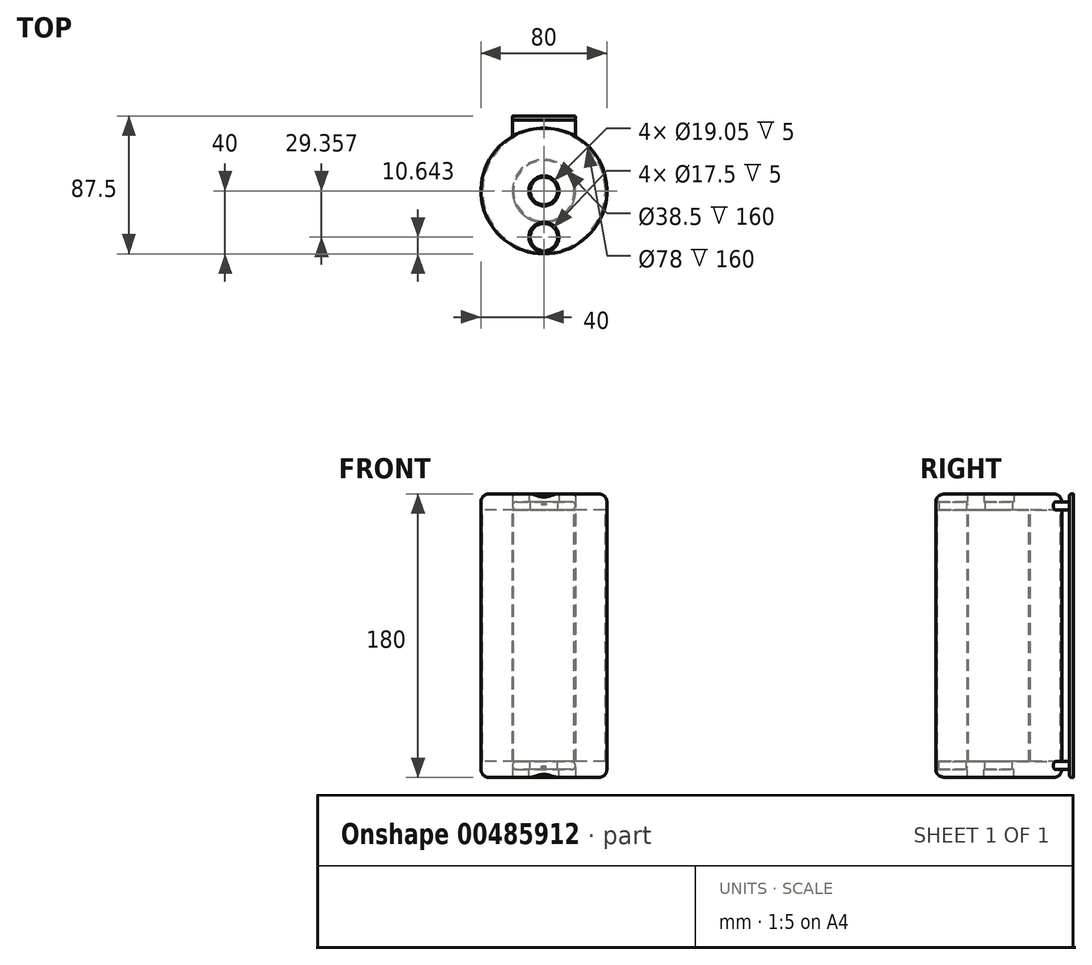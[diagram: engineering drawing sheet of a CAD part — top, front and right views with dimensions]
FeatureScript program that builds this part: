
annotation { "Feature Type Name" : "Feature", "Feature Type Description" : "" }
export const myFeature = defineFeature(function(context is Context, id is Id, definition is map)
    precondition{}
    {
        {
            var Q0;
            Q0=qCreatedBy(makeId("Top.planeOp"),FACE);
            var sketch = newSketch(context, id + "F0", { "sketchPlane" : qUnion([Q0])});
            skCircle(sketch, "E0", {"center": v(0, 0) * mm, "radius": 40 * mm});
            skLineSegment(sketch, "E1", {"start": v(0, 0) * mm, "end": v(0, -20) * mm});
            skLineSegment(sketch, "E2", {"start": v(0, -20) * mm, "end": v(0, -21.21) * mm});
            skLineSegment(sketch, "E3", {"start": v(0, -21.21) * mm, "end": v(0, -37.5) * mm});
            skLineSegment(sketch, "E4", {"start": v(0, -37.5) * mm, "end": v(0, -29.36) * mm});
            skCircle(sketch, "E5", {"center": v(0, -29.36) * mm, "radius": 9.53 * mm});
            skCircle(sketch, "E6", {"center": v(0, 0) * mm, "radius": 9.53 * mm});
            skCircle(sketch, "E7", {"center": v(0, 0) * mm, "radius": 20 * mm});
            skCircle(sketch, "E8", {"center": v(0, 0) * mm, "radius": 19.25 * mm});
            skCircle(sketch, "E9", {"center": v(0, -29.36) * mm, "radius": 8.75 * mm});
            skCircle(sketch, "E10", {"center": v(0, 0) * mm, "radius": 8.75 * mm});
            skCircle(sketch, "E11", {"center": v(0, 0) * mm, "radius": 39 * mm});
            skLineSegment(sketch, "E12.top", {"start": v(20, 40) * mm, "end": v(0, 40) * mm});
            skLineSegment(sketch, "E13.top", {"start": v(0, 40) * mm, "end": v(-20, 40) * mm});
            skLineSegment(sketch, "E14", {"start": v(-20, 34.64) * mm, "end": v(-20, 40) * mm});
            skLineSegment(sketch, "E15", {"start": v(20, 40) * mm, "end": v(20, 34.64) * mm});
            skLineSegment(sketch, "E16.bottom", {"start": v(-20, 40) * mm, "end": v(20, 40) * mm});
            skLineSegment(sketch, "E16.top", {"start": v(-20, 45) * mm, "end": v(20, 45) * mm});
            skLineSegment(sketch, "E16.left", {"start": v(-20, 40) * mm, "end": v(-20, 45) * mm});
            skLineSegment(sketch, "E16.right", {"start": v(20, 40) * mm, "end": v(20, 45) * mm});
            skLineSegment(sketch, "E17.top", {"start": v(-20, 47.5) * mm, "end": v(20, 47.5) * mm});
            skLineSegment(sketch, "E17.left", {"start": v(-20, 45) * mm, "end": v(-20, 47.5) * mm});
            skLineSegment(sketch, "E17.right", {"start": v(20, 45) * mm, "end": v(20, 47.5) * mm});
            skSolve(sketch);
        }
        {
            var Q0;
            Q0=makeQuery(id+"F0.imprint","IMPRINT",FACE,{"disambiguationData":[TD([[makeQuery(id+"F0.imprint","IMPRINT",EDGE,{"derivedFrom":sQuery(id+"F0.wireOp",EDGE,"E11")}),1.0]])]});
            var Q1;
            Q1=makeQuery(id+"F0.imprint","IMPRINT",FACE,{"disambiguationData":[TD([[makeQuery(id+"F0.imprint","IMPRINT",EDGE,{"derivedFrom":sQuery(id+"F0.wireOp",EDGE,"E11")}),-1.0]])]});
            var Q2;
            Q2=makeQuery(id+"F0.imprint","IMPRINT",FACE,{"disambiguationData":[TD([[makeQuery(id+"F0.imprint","IMPRINT",EDGE,{"derivedFrom":sQuery(id+"F0.wireOp",EDGE,"E6")}),1.0]])]});
            var Q3;
            Q3=makeQuery(id+"F0.imprint","IMPRINT",FACE,{"disambiguationData":[TD([[makeQuery(id+"F0.imprint","IMPRINT",EDGE,{"derivedFrom":sQuery(id+"F0.wireOp",EDGE,"E6")}),-1.0]])]});
            var Q4;
            Q4=makeQuery(id+"F0.imprint","IMPRINT",FACE,{"disambiguationData":[TD([[makeQuery(id+"F0.imprint","IMPRINT",EDGE,{"derivedFrom":sQuery(id+"F0.wireOp",EDGE,"E8")}),-1.0]])]});
            var Q5;
            Q5=makeQuery(id+"F0.imprint","IMPRINT",FACE,{"disambiguationData":[TD([[makeQuery(id+"F0.imprint","IMPRINT",EDGE,{"derivedFrom":sQuery(id+"F0.wireOp",EDGE,"E9")}),-1.0]])]});
            extrude(context, id + "F1", {"entities" : qUnion([Q0, Q1, Q2, Q3, Q4, Q5]), "oppositeDirection" : true, "depth" : 10 * mm});
        }
        {
            var Q0;
            Q0=qSketchRegion(id+"FNYP8afO0flnPvm_4",true);
            var Q1;
            Q1=makeQuery(id+"F0.imprint","IMPRINT",FACE,{"disambiguationData":[TD([[makeQuery(id+"F0.imprint","IMPRINT",EDGE,{"derivedFrom":sQuery(id+"F0.wireOp",EDGE,"E11")}),-1.0]])]});
            var Q2;
            Q2=makeQuery(id+"F0.imprint","IMPRINT",FACE,{"disambiguationData":[TD([[makeQuery(id+"F0.imprint","IMPRINT",EDGE,{"derivedFrom":sQuery(id+"F0.wireOp",EDGE,"E8")}),-1.0]])]});
            extrude(context, id + "F2", {"entities" : qUnion([Q0, Q1, Q2]), "operationType" : NewBodyOperationType.REMOVE, "oppositeDirection" : true, "depth" : 4 * mm});
        }
        {
            var Q0;
            Q0=makeQuery(id+"F0.imprint","IMPRINT",FACE,{"disambiguationData":[TD([[makeQuery(id+"F0.imprint","IMPRINT",EDGE,{"derivedFrom":sQuery(id+"F0.wireOp",EDGE,"E6")}),1.0]])]});
            var Q1;
            {var subQ0=sQuery(id+"F0.wireOp",EDGE,"E7");var subQ1=sQuery(id+"F0.wireOp",EDGE,"E1");var subQ2=makeQuery(id+"F0.imprint","INTERSECT",VERTEX,{"derivedFrom":[subQ1,subQ0]});Q1=makeQuery(id+"F0.imprint","IMPRINT",FACE,{"disambiguationData":[TD([[makeQuery(id+"F0.imprint","IMPRINT",EDGE,{"disambiguationData":[TD([[subQ2,1.0]])],"derivedFrom":subQ1}),1.0]])]});}
            var Q2;
            {var subQ0=sQuery(id+"F0.wireOp",EDGE,"E7");var subQ1=sQuery(id+"F0.wireOp",EDGE,"E1");var subQ2=makeQuery(id+"F0.imprint","INTERSECT",VERTEX,{"derivedFrom":[subQ1,subQ0]});Q2=makeQuery(id+"F0.imprint","IMPRINT",FACE,{"disambiguationData":[TD([[makeQuery(id+"F0.imprint","IMPRINT",EDGE,{"disambiguationData":[TD([[subQ2,1.0]])],"derivedFrom":subQ1}),-1.0]])]});}
            var Q3;
            Q3=makeQuery(id+"F0.imprint","IMPRINT",FACE,{"disambiguationData":[TD([[makeQuery(id+"F0.imprint","IMPRINT",EDGE,{"derivedFrom":sQuery(id+"F0.wireOp",EDGE,"E9")}),-1.0]])]});
            extrude(context, id + "F3", {"entities" : qUnion([Q0, Q1, Q2, Q3]), "operationType" : NewBodyOperationType.REMOVE, "oppositeDirection" : true, "depth" : 10 * mm, "hasSecondDirection" : true, "secondDirectionOppositeDirection" : true, "secondDirectionDepth" : 5 * mm});
        }
        {
            var Q0;
            Q0=makeQuery(id+"F1.opExtrude","CAP_EDGE",EDGE,{"disambiguationData":[OSD([sQuery(id+"F0.wireOp",EDGE,"E0")])],"isStart":false});
            fillet(context, id + "F4", {"entities" : qUnion([Q0]), "radius" : 5 * mm, "tangentPropagation" : true, "allowEdgeOverflow" : false});
        }
        {
            var Q0;
            {var subQ0=sQuery(id+"F0.wireOp",EDGE,"E7");var subQ1=sQuery(id+"F0.wireOp",EDGE,"E1");var subQ2=makeQuery(id+"F0.imprint","INTERSECT",VERTEX,{"derivedFrom":[subQ1,subQ0]});Q0=makeQuery(id+"F0.imprint","IMPRINT",FACE,{"disambiguationData":[TD([[makeQuery(id+"F0.imprint","IMPRINT",EDGE,{"disambiguationData":[TD([[subQ2,1.0]])],"derivedFrom":subQ1}),-1.0]])]});}
            var Q1;
            {var subQ0=sQuery(id+"F0.wireOp",EDGE,"E7");var subQ1=sQuery(id+"F0.wireOp",EDGE,"E1");var subQ2=makeQuery(id+"F0.imprint","INTERSECT",VERTEX,{"derivedFrom":[subQ1,subQ0]});Q1=makeQuery(id+"F0.imprint","IMPRINT",FACE,{"disambiguationData":[TD([[makeQuery(id+"F0.imprint","IMPRINT",EDGE,{"disambiguationData":[TD([[subQ2,1.0]])],"derivedFrom":subQ1}),1.0]])]});}
            extrude(context, id + "F5", {"entities" : qUnion([Q0, Q1]), "operationType" : NewBodyOperationType.ADD, "oppositeDirection" : true, "depth" : 5 * mm, "hasSecondDirection" : true, "secondDirectionOppositeDirection" : true, "secondDirectionDepth" : 4 * mm});
        }
        {
            var Q0;
            Q0=makeQuery(id+"F0.imprint","IMPRINT",FACE,{"disambiguationData":[TD([[makeQuery(id+"F0.imprint","IMPRINT",EDGE,{"derivedFrom":sQuery(id+"F0.wireOp",EDGE,"E11")}),-1.0]])]});
            var Q1;
            Q1=makeQuery(id+"F0.imprint","IMPRINT",FACE,{"disambiguationData":[TD([[makeQuery(id+"F0.imprint","IMPRINT",EDGE,{"derivedFrom":sQuery(id+"F0.wireOp",EDGE,"E8")}),-1.0]])]});
            extrude(context, id + "F6", {"entities" : qUnion([Q0, Q1]), "oppositeDirection" : true, "depth" : 4 * mm, "hasSecondDirection" : true, "secondDirectionOppositeDirection" : true, "secondDirectionDepth" : 3 * mm});
        }
        {
            var Q0;
            Q0=makeQuery(id+"F0.imprint","IMPRINT",FACE,{"disambiguationData":[TD([[makeQuery(id+"F0.imprint","IMPRINT",EDGE,{"derivedFrom":sQuery(id+"F0.wireOp",EDGE,"E11")}),-1.0]])]});
            var Q1;
            Q1=makeQuery(id+"F0.imprint","IMPRINT",FACE,{"disambiguationData":[TD([[makeQuery(id+"F0.imprint","IMPRINT",EDGE,{"derivedFrom":sQuery(id+"F0.wireOp",EDGE,"E8")}),-1.0]])]});
            var Q2;
            {var subQ0=sQuery(id+"F0.wireOp",EDGE,"E7");var subQ1=sQuery(id+"F0.wireOp",EDGE,"E1");var subQ2=makeQuery(id+"F0.imprint","INTERSECT",VERTEX,{"derivedFrom":[subQ1,subQ0]});Q2=makeQuery(id+"F0.imprint","IMPRINT",FACE,{"disambiguationData":[TD([[makeQuery(id+"F0.imprint","IMPRINT",EDGE,{"disambiguationData":[TD([[subQ2,1.0]])],"derivedFrom":subQ1}),1.0]])]});}
            var Q3;
            {var subQ0=sQuery(id+"F0.wireOp",EDGE,"E7");var subQ1=sQuery(id+"F0.wireOp",EDGE,"E1");var subQ2=makeQuery(id+"F0.imprint","INTERSECT",VERTEX,{"derivedFrom":[subQ1,subQ0]});Q3=makeQuery(id+"F0.imprint","IMPRINT",FACE,{"disambiguationData":[TD([[makeQuery(id+"F0.imprint","IMPRINT",EDGE,{"disambiguationData":[TD([[subQ2,1.0]])],"derivedFrom":subQ1}),-1.0]])]});}
            extrude(context, id + "F7", {"entities" : qUnion([Q0, Q1, Q2, Q3]), "depth" : 80 * mm, "hasSecondDirection" : true, "secondDirectionOppositeDirection" : true, "secondDirectionDepth" : 3 * mm});
        }
        {
            var Q0;
            Q0=makeQuery(id+"F7.opExtrude","SWEPT_BODY",BODY,{"disambiguationData":[OSD([sQuery(id+"F0.wireOp",EDGE,"E7"),sQuery(id+"F0.wireOp",EDGE,"E8")])]});
            var Q1;
            Q1=makeQuery(id+"F7.opExtrude","CAP_FACE",FACE,{"disambiguationData":[OSD([sQuery(id+"F0.wireOp",EDGE,"E7"),sQuery(id+"F0.wireOp",EDGE,"E8")])],"isStart":false});
            mirror(context, id + "F8", {"operationType" : NewBodyOperationType.ADD, "entities" : qUnion([Q0]), "mirrorPlane" : qUnion([Q1])});
        }
        {
            var Q0;
            Q0=makeQuery(id+"F1.opExtrude","SWEPT_BODY",BODY,{"disambiguationData":[OSD([sQuery(id+"F0.wireOp",EDGE,"E0"),sQuery(id+"F0.wireOp",EDGE,"E5"),sQuery(id+"F0.wireOp",EDGE,"E7"),sQuery(id+"F0.wireOp",EDGE,"E9"),sQuery(id+"F0.wireOp",EDGE,"E10")])]});
            var Q1;
            Q1=makeQuery(id+"F6.opExtrude","SWEPT_BODY",BODY,{"disambiguationData":[OSD([sQuery(id+"F0.wireOp",EDGE,"E0"),sQuery(id+"F0.wireOp",EDGE,"E11")])]});
            var Q2;
            Q2=makeQuery(id+"F6.opExtrude","SWEPT_BODY",BODY,{"disambiguationData":[OSD([sQuery(id+"F0.wireOp",EDGE,"E5"),sQuery(id+"F0.wireOp",EDGE,"E7"),sQuery(id+"F0.wireOp",EDGE,"E8")])]});
            var Q3;
            Q3=makeQuery(id+"F7.opExtrude","CAP_FACE",FACE,{"disambiguationData":[OSD([sQuery(id+"F0.wireOp",EDGE,"E0"),sQuery(id+"F0.wireOp",EDGE,"E11")])],"isStart":false});
            mirror(context, id + "F9", {"entities" : qUnion([Q0, Q1, Q2]), "mirrorPlane" : qUnion([Q3])});
        }
        {
            var Q0;
            Q0=makeQuery(id+"F7.opExtrude","SWEPT_BODY",BODY,{"disambiguationData":[OSD([sQuery(id+"F0.wireOp",EDGE,"E0"),sQuery(id+"F0.wireOp",EDGE,"E11")])]});
            var Q1;
            Q1=makeQuery(id+"F7.opExtrude","CAP_FACE",FACE,{"disambiguationData":[OSD([sQuery(id+"F0.wireOp",EDGE,"E0"),sQuery(id+"F0.wireOp",EDGE,"E11")])],"isStart":false});
            mirror(context, id + "F10", {"operationType" : NewBodyOperationType.ADD, "entities" : qUnion([Q0]), "mirrorPlane" : qUnion([Q1])});
        }
        {
            var Q0;
            {var subQ0=sQuery(id+"F0.wireOp",EDGE,"E15");Q0=makeQuery(id+"F0.imprint","IMPRINT",FACE,{"disambiguationData":[TD([[makeQuery(id+"F0.imprint","IMPRINT",EDGE,{"derivedFrom":subQ0}),-1.0]])]});}
            var Q1;
            {var subQ0=sQuery(id+"F0.wireOp",EDGE,"E14");Q1=makeQuery(id+"F0.imprint","IMPRINT",FACE,{"disambiguationData":[TD([[makeQuery(id+"F0.imprint","IMPRINT",EDGE,{"derivedFrom":subQ0}),-1.0]])]});}
            var Q2;
            Q2=makeQuery(id+"F0.imprint","IMPRINT",FACE,{"disambiguationData":[TD([[makeQuery(id+"F0.imprint","IMPRINT",EDGE,{"derivedFrom":sQuery(id+"F0.wireOp",EDGE,"E16.top")}),-1.0]])]});
            extrude(context, id + "F11", {"entities" : qUnion([Q0, Q1, Q2]), "depth" : 165 * mm, "hasSecondDirection" : true, "secondDirectionOppositeDirection" : false, "secondDirectionDepth" : 160 * mm});
        }
        {
            var Q0;
            Q0=makeQuery(id+"F1KWkgZxmQ7jtSi_5.opExtrude","CAP_EDGE",EDGE,{"disambiguationData":[OSD([sQuery(id+"F0.wireOp",EDGE,"E14"),sQuery(id+"F0.wireOp",EDGE,"E16.left")])],"isStart":true});
            var Q1;
            Q1=makeQuery(id+"F1KWkgZxmQ7jtSi_5.opExtrude","CAP_EDGE",EDGE,{"disambiguationData":[OSD([sQuery(id+"F0.wireOp",EDGE,"E15"),sQuery(id+"F0.wireOp",EDGE,"E16.right")])],"isStart":true});
            var Q2;
            Q2=makeQuery(id+"F1KWkgZxmQ7jtSi_5.opExtrude","CAP_EDGE",EDGE,{"disambiguationData":[OSD([sQuery(id+"F0.wireOp",EDGE,"E15"),sQuery(id+"F0.wireOp",EDGE,"E16.right")])],"isStart":false});
            var Q3;
            Q3=makeQuery(id+"F1KWkgZxmQ7jtSi_5.opExtrude","CAP_EDGE",EDGE,{"disambiguationData":[OSD([sQuery(id+"F0.wireOp",EDGE,"E14"),sQuery(id+"F0.wireOp",EDGE,"E16.left")])],"isStart":false});
            var Q4;
            Q4=makeQuery(id+"F11.opExtrude","CAP_EDGE",EDGE,{"disambiguationData":[OSD([sQuery(id+"F0.wireOp",EDGE,"E14"),sQuery(id+"F0.wireOp",EDGE,"E16.left")])],"isStart":true});
            var Q5;
            Q5=makeQuery(id+"F11.opExtrude","CAP_EDGE",EDGE,{"disambiguationData":[OSD([sQuery(id+"F0.wireOp",EDGE,"E15"),sQuery(id+"F0.wireOp",EDGE,"E16.right")])],"isStart":true});
            var Q6;
            Q6=makeQuery(id+"F11.opExtrude","CAP_EDGE",EDGE,{"disambiguationData":[OSD([sQuery(id+"F0.wireOp",EDGE,"E15"),sQuery(id+"F0.wireOp",EDGE,"E16.right")])],"isStart":false});
            var Q7;
            Q7=makeQuery(id+"F11.opExtrude","CAP_EDGE",EDGE,{"disambiguationData":[OSD([sQuery(id+"F0.wireOp",EDGE,"E14"),sQuery(id+"F0.wireOp",EDGE,"E16.left")])],"isStart":false});
            fillet(context, id + "F12", {"entities" : qUnion([Q0, Q1, Q2, Q3, Q4, Q5, Q6, Q7]), "radius" : 2.5 * mm, "tangentPropagation" : true, "allowEdgeOverflow" : false});
        }
        {
            var Q0;
            {var subQ1=sQuery(id+"F0.wireOp",EDGE,"E16.left");Q0=makeQuery(id+"F0.imprint","IMPRINT",FACE,{"disambiguationData":[TD([[makeQuery(id+"F0.imprint","IMPRINT",EDGE,{"derivedFrom":subQ1}),-1.0]])]});}
            var Q1;
            {var subQ0=sQuery(id+"F0.wireOp",EDGE,"E14");Q1=makeQuery(id+"F0.imprint","IMPRINT",FACE,{"disambiguationData":[TD([[makeQuery(id+"F0.imprint","IMPRINT",EDGE,{"derivedFrom":subQ0}),-1.0]])]});}
            var Q2;
            {var subQ0=sQuery(id+"F0.wireOp",EDGE,"E15");Q2=makeQuery(id+"F0.imprint","IMPRINT",FACE,{"disambiguationData":[TD([[makeQuery(id+"F0.imprint","IMPRINT",EDGE,{"derivedFrom":subQ0}),-1.0]])]});}
            extrude(context, id + "F13", {"entities" : qUnion([Q0, Q1, Q2]), "operationType" : NewBodyOperationType.ADD, "oppositeDirection" : true, "depth" : 5 * mm});
        }
        {
            var Q0;
            Q0=makeQuery(id+"F13.opExtrude","CAP_EDGE",EDGE,{"disambiguationData":[OSD([sQuery(id+"F0.wireOp",EDGE,"E15"),sQuery(id+"F0.wireOp",EDGE,"E16.right")])],"isStart":false});
            var Q1;
            Q1=makeQuery(id+"F13.opExtrude","CAP_EDGE",EDGE,{"disambiguationData":[OSD([sQuery(id+"F0.wireOp",EDGE,"E15"),sQuery(id+"F0.wireOp",EDGE,"E16.right")])],"isStart":true});
            var Q2;
            Q2=makeQuery(id+"F13.opExtrude","CAP_EDGE",EDGE,{"disambiguationData":[OSD([sQuery(id+"F0.wireOp",EDGE,"E14"),sQuery(id+"F0.wireOp",EDGE,"E16.left")])],"isStart":false});
            var Q3;
            Q3=makeQuery(id+"F13.opExtrude","CAP_EDGE",EDGE,{"disambiguationData":[OSD([sQuery(id+"F0.wireOp",EDGE,"E14"),sQuery(id+"F0.wireOp",EDGE,"E16.left")])],"isStart":true});
            fillet(context, id + "F14", {"entities" : qUnion([Q0, Q1, Q2, Q3]), "radius" : 2.5 * mm, "tangentPropagation" : true, "allowEdgeOverflow" : false});
        }
        {
            var Q0;
            {var subQ1=sQuery(id+"F0.wireOp",EDGE,"E16.left");Q0=makeQuery(id+"F0.imprint","IMPRINT",FACE,{"disambiguationData":[TD([[makeQuery(id+"F0.imprint","IMPRINT",EDGE,{"derivedFrom":subQ1}),-1.0]])]});}
            extrude(context, id + "F15", {"entities" : qUnion([Q0]), "operationType" : NewBodyOperationType.ADD, "depth" : 165 * mm, "hasSecondDirection" : true, "secondDirectionOppositeDirection" : false, "secondDirectionDepth" : 160 * mm});
        }
        {
            var Q0;
            Q0=makeQuery(id+"F15.opExtrude","CAP_EDGE",EDGE,{"disambiguationData":[OSD([sQuery(id+"F0.wireOp",EDGE,"E16.left")])],"isStart":false});
            var Q1;
            Q1=makeQuery(id+"F15.opExtrude","CAP_EDGE",EDGE,{"disambiguationData":[OSD([sQuery(id+"F0.wireOp",EDGE,"E16.left")])],"isStart":true});
            var Q2;
            Q2=makeQuery(id+"F15.opExtrude","CAP_EDGE",EDGE,{"disambiguationData":[OSD([sQuery(id+"F0.wireOp",EDGE,"E16.right")])],"isStart":false});
            var Q3;
            Q3=makeQuery(id+"F15.opExtrude","CAP_EDGE",EDGE,{"disambiguationData":[OSD([sQuery(id+"F0.wireOp",EDGE,"E16.right")])],"isStart":true});
            fillet(context, id + "F16", {"entities" : qUnion([Q0, Q1, Q2, Q3]), "radius" : 2.5 * mm, "tangentPropagation" : true, "allowEdgeOverflow" : false});
        }
        {
            var Q0;
            Q0=makeQuery(id+"F0.imprint","IMPRINT",FACE,{"disambiguationData":[TD([[makeQuery(id+"F0.imprint","IMPRINT",EDGE,{"derivedFrom":sQuery(id+"F0.wireOp",EDGE,"E16.top")}),1.0]])]});
            extrude(context, id + "F17", {"entities" : qUnion([Q0]), "depth" : 170 * mm, "hasSecondDirection" : true, "secondDirectionOppositeDirection" : true, "secondDirectionDepth" : 10 * mm});
        }
        {
            var Q0;
            Q0=makeQuery(id+"F17.opExtrude","SWEPT_EDGE",EDGE,{"disambiguationData":[OSD([sQuery(id+"F0.wireOp",EDGE,"E16.left"),sQuery(id+"F0.wireOp",EDGE,"E16.top"),sQuery(id+"F0.wireOp",EDGE,"E17.left")])]});
            var Q1;
            Q1=makeQuery(id+"F17.opExtrude","CAP_EDGE",EDGE,{"disambiguationData":[OSD([sQuery(id+"F0.wireOp",EDGE,"E16.top")])],"isStart":true});
            var Q2;
            Q2=makeQuery(id+"F17.opExtrude","SWEPT_EDGE",EDGE,{"disambiguationData":[OSD([sQuery(id+"F0.wireOp",EDGE,"E16.right"),sQuery(id+"F0.wireOp",EDGE,"E16.top"),sQuery(id+"F0.wireOp",EDGE,"E17.right")])]});
            var Q3;
            Q3=makeQuery(id+"F17.opExtrude","CAP_EDGE",EDGE,{"disambiguationData":[OSD([sQuery(id+"F0.wireOp",EDGE,"E16.top")])],"isStart":false});
            var Q4;
            Q4=makeQuery(id+"F17.opExtrude","CAP_EDGE",EDGE,{"disambiguationData":[OSD([sQuery(id+"F0.wireOp",EDGE,"E17.right")])],"isStart":false});
            var Q5;
            Q5=makeQuery(id+"F17.opExtrude","CAP_EDGE",EDGE,{"disambiguationData":[OSD([sQuery(id+"F0.wireOp",EDGE,"E17.left")])],"isStart":false});
            var Q6;
            Q6=makeQuery(id+"F17.opExtrude","CAP_EDGE",EDGE,{"disambiguationData":[OSD([sQuery(id+"F0.wireOp",EDGE,"E17.left")])],"isStart":true});
            var Q7;
            Q7=makeQuery(id+"F17.opExtrude","CAP_EDGE",EDGE,{"disambiguationData":[OSD([sQuery(id+"F0.wireOp",EDGE,"E17.right")])],"isStart":true});
            fillet(context, id + "F18", {"entities" : qUnion([Q0, Q1, Q2, Q3, Q4, Q5, Q6, Q7]), "radius" : 1 * mm, "tangentPropagation" : true, "allowEdgeOverflow" : false});
        }
    });
